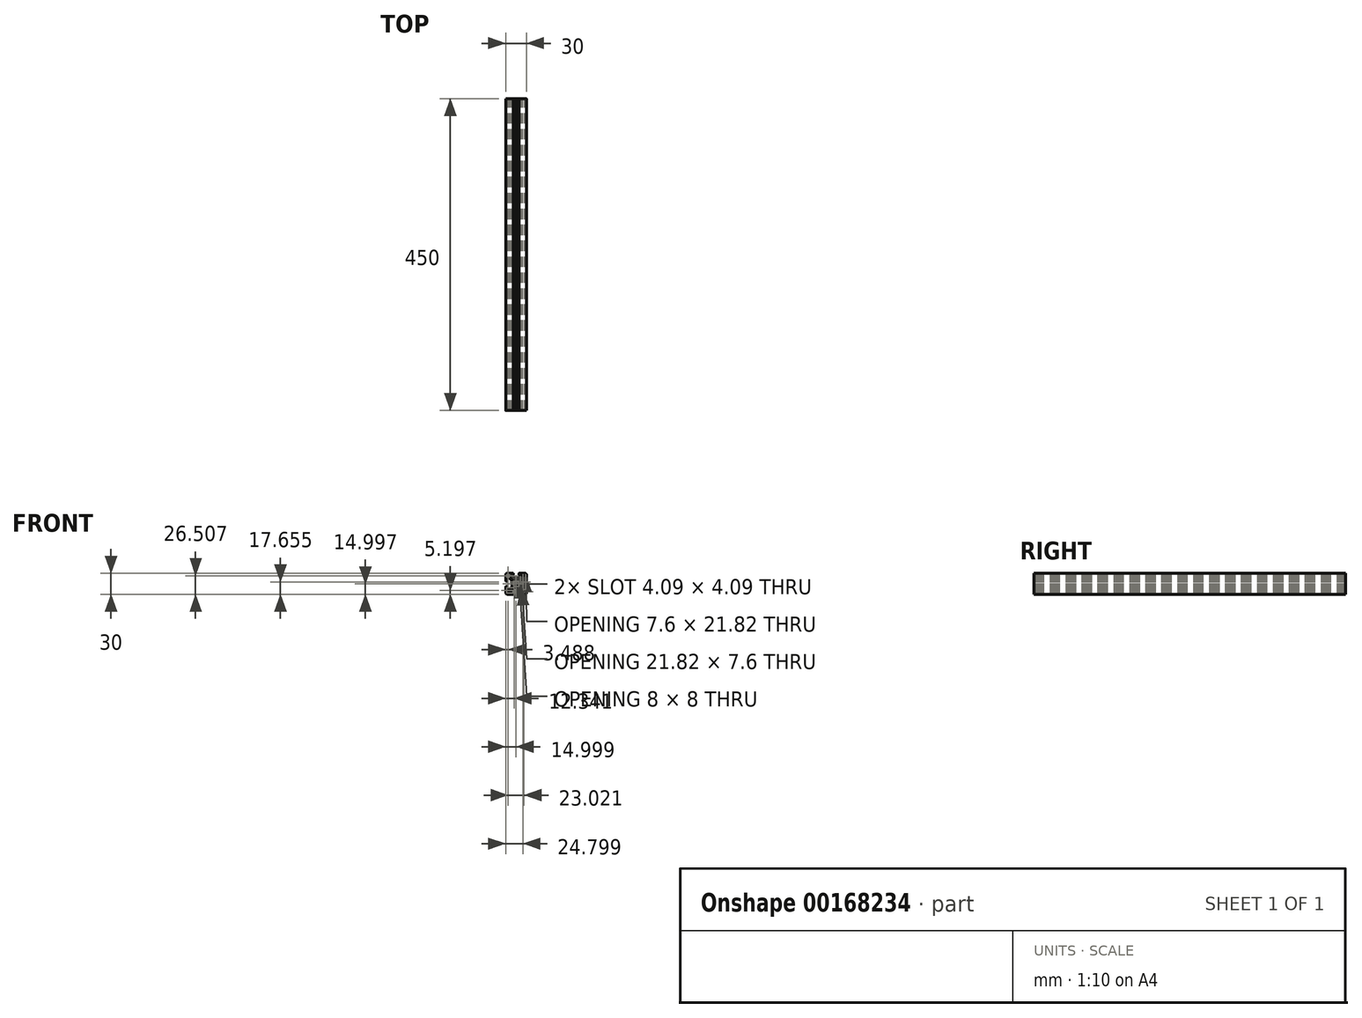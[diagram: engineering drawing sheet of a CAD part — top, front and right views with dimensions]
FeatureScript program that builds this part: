
annotation { "Feature Type Name" : "Feature", "Feature Type Description" : "" }
export const myFeature = defineFeature(function(context is Context, id is Id, definition is map)
    precondition{}
    {
        {
            var Q0;
            Q0=qCreatedBy(makeId("Front.planeOp"),FACE);
            var sketch = newSketch(context, id + "F0", { "sketchPlane" : qUnion([Q0])});
            skLineSegment(sketch, "E0", {"start": v(-39.84, 24.25) * mm, "end": v(-39.84, -9.75) * mm});
            skLineSegment(sketch, "E1", {"start": v(-56.84, 7.25) * mm, "end": v(-22.84, 7.25) * mm});
            skLineSegment(sketch, "E2", {"start": v(-52.84, 22.25) * mm, "end": v(-44.14, 22.25) * mm});
            skLineSegment(sketch, "E3", {"start": v(-52.84, -7.75) * mm, "end": v(-26.84, -7.75) * mm});
            skLineSegment(sketch, "E4", {"start": v(-24.84, 20.25) * mm, "end": v(-24.84, -5.75) * mm});
            skLineSegment(sketch, "E5", {"start": v(-54.84, 20.25) * mm, "end": v(-54.84, 11.55) * mm});
            skArc(sketch, "E6", {"start": v(-24.84, 20.25) * mm, "mid": v(-25.43, 21.66) * mm, "end": v(-26.84, 22.25) * mm});
            skArc(sketch, "E7", {"start": v(-52.84, 22.25) * mm, "mid": v(-54.26, 21.66) * mm, "end": v(-54.84, 20.25) * mm});
            skArc(sketch, "E8", {"start": v(-54.84, -5.75) * mm, "mid": v(-54.26, -7.17) * mm, "end": v(-52.84, -7.75) * mm});
            skArc(sketch, "E9", {"start": v(-26.84, -7.75) * mm, "mid": v(-25.43, -7.17) * mm, "end": v(-24.84, -5.75) * mm});
            skLineSegment(sketch, "E10", {"start": v(-52.84, -1) * mm, "end": v(-52.84, 2.95) * mm});
            skLineSegment(sketch, "E11", {"start": v(-26.84, 15.44) * mm, "end": v(-26.84, 0) * mm});
            skLineSegment(sketch, "E12", {"start": v(-48.03, -5.75) * mm, "end": v(-32.6, -5.75) * mm});
            skLineSegment(sketch, "E13", {"start": v(-54.54, 3.25) * mm, "end": v(-53.14, 3.25) * mm});
            skLineSegment(sketch, "E14", {"start": v(-54.54, 11.25) * mm, "end": v(-53.14, 11.25) * mm});
            skLineSegment(sketch, "E15", {"start": v(-52.84, 11.55) * mm, "end": v(-52.84, 15.5) * mm});
            skLineSegment(sketch, "E16", {"start": v(-35.54, 22.25) * mm, "end": v(-26.84, 22.25) * mm});
            skLineSegment(sketch, "E17", {"start": v(-49.5, -1) * mm, "end": v(-52.84, -1) * mm});
            skLineSegment(sketch, "E18", {"start": v(-49.5, 15.5) * mm, "end": v(-52.84, 15.5) * mm});
            skLineSegment(sketch, "E19", {"start": v(-35.26, 13.25) * mm, "end": v(-39.19, 13.25) * mm});
            skLineSegment(sketch, "E20", {"start": v(-35.67, 1.25) * mm, "end": v(-44.01, 1.25) * mm});
            skLineSegment(sketch, "E21", {"start": v(-33.84, 3.08) * mm, "end": v(-33.84, 11.42) * mm});
            skLineSegment(sketch, "E22", {"start": v(-45.84, 2.66) * mm, "end": v(-45.84, 4.75) * mm});
            skLineSegment(sketch, "E23", {"start": v(-44.43, 13.25) * mm, "end": v(-48.1, 16.91) * mm});
            skLineSegment(sketch, "E24", {"start": v(-45.84, 11.83) * mm, "end": v(-49.5, 15.5) * mm});
            skLineSegment(sketch, "E25", {"start": v(-33.55, 12.13) * mm, "end": v(-30.68, 14.99) * mm});
            skLineSegment(sketch, "E26", {"start": v(-35.26, 13.25) * mm, "end": v(-31.6, 16.91) * mm});
            skLineSegment(sketch, "E27", {"start": v(-33.55, 2.37) * mm, "end": v(-30.47, -0.71) * mm});
            skLineSegment(sketch, "E28", {"start": v(-34.96, 0.95) * mm, "end": v(-31.88, -2.12) * mm});
            skLineSegment(sketch, "E29", {"start": v(-44.72, 0.95) * mm, "end": v(-47.58, -1.91) * mm});
            skLineSegment(sketch, "E30", {"start": v(-45.84, 2.66) * mm, "end": v(-49.5, -1) * mm});
            skLineSegment(sketch, "E31", {"start": v(-54.84, 2.95) * mm, "end": v(-54.84, -5.75) * mm});
            skLineSegment(sketch, "E32", {"start": v(-43.84, 21.95) * mm, "end": v(-43.84, 20.55) * mm});
            skLineSegment(sketch, "E33", {"start": v(-35.84, 21.95) * mm, "end": v(-35.84, 20.55) * mm});
            skLineSegment(sketch, "E34", {"start": v(-31.6, 16.91) * mm, "end": v(-31.6, 20.25) * mm});
            skLineSegment(sketch, "E35", {"start": v(-48.1, 16.91) * mm, "end": v(-48.1, 20.25) * mm});
            skLineSegment(sketch, "E36", {"start": v(-44.14, 20.25) * mm, "end": v(-48.1, 20.25) * mm});
            skLineSegment(sketch, "E37", {"start": v(-35.54, 20.25) * mm, "end": v(-31.6, 20.25) * mm});
            skLineSegment(sketch, "E38", {"start": v(-30.4, 15.7) * mm, "end": v(-30.4, 18.32) * mm});
            skLineSegment(sketch, "E39", {"start": v(-30.4, 18.32) * mm, "end": v(-29.93, 19.6) * mm});
            skArc(sketch, "E40", {"start": v(-27.06, 17.38) * mm, "mid": v(-26.98, 20.45) * mm, "end": v(-29.93, 19.6) * mm});
            skArc(sketch, "E41", {"start": v(-27.06, 17.38) * mm, "mid": v(-27.5, 16.52) * mm, "end": v(-27, 15.7) * mm});
            skArc(sketch, "E42", {"start": v(-26.84, 15.44) * mm, "mid": v(-26.88, 15.59) * mm, "end": v(-27, 15.7) * mm});
            skArc(sketch, "E43", {"start": v(-49.76, 19.6) * mm, "mid": v(-52.88, 20.3) * mm, "end": v(-52.2, 17.16) * mm});
            skLineSegment(sketch, "E44", {"start": v(-49.39, 18.59) * mm, "end": v(-49.76, 19.6) * mm});
            skLineSegment(sketch, "E45", {"start": v(-51.18, 16.8) * mm, "end": v(-52.2, 17.16) * mm});
            skArc(sketch, "E46", {"start": v(-51.18, 16.8) * mm, "mid": v(-49.71, 17.12) * mm, "end": v(-49.39, 18.59) * mm});
            skArc(sketch, "E47", {"start": v(-29.93, -5.1) * mm, "mid": v(-26.8, -5.8) * mm, "end": v(-27.5, -2.67) * mm});
            skLineSegment(sketch, "E48", {"start": v(-28.5, -2.3) * mm, "end": v(-27.5, -2.67) * mm});
            skLineSegment(sketch, "E49", {"start": v(-30.3, -4.1) * mm, "end": v(-29.93, -5.1) * mm});
            skArc(sketch, "E50", {"start": v(-28.5, -2.3) * mm, "mid": v(-29.97, -2.63) * mm, "end": v(-30.3, -4.1) * mm});
            skArc(sketch, "E51", {"start": v(-33.55, 12.13) * mm, "mid": v(-33.76, 11.8) * mm, "end": v(-33.84, 11.42) * mm});
            skArc(sketch, "E52", {"start": v(-33.84, 3.08) * mm, "mid": v(-33.76, 2.7) * mm, "end": v(-33.55, 2.37) * mm});
            skLineSegment(sketch, "E53", {"start": v(-29.76, -1) * mm, "end": v(-27.84, -1) * mm});
            skArc(sketch, "E54", {"start": v(-30.47, -0.71) * mm, "mid": v(-30.15, -0.93) * mm, "end": v(-29.76, -1) * mm});
            skArc(sketch, "E55", {"start": v(-27.84, -1) * mm, "mid": v(-27.13, -0.71) * mm, "end": v(-26.84, 0) * mm});
            skArc(sketch, "E56", {"start": v(-30.68, 14.99) * mm, "mid": v(-30.47, 15.31) * mm, "end": v(-30.4, 15.7) * mm});
            skLineSegment(sketch, "E57", {"start": v(-31.6, -2.83) * mm, "end": v(-31.6, -4.75) * mm});
            skLineSegment(sketch, "E58", {"start": v(-48.3, -2.2) * mm, "end": v(-50.91, -2.2) * mm});
            skLineSegment(sketch, "E59", {"start": v(-50.91, -2.2) * mm, "end": v(-52.2, -2.67) * mm});
            skArc(sketch, "E60", {"start": v(-52.2, -2.67) * mm, "mid": v(-53.04, -5.61) * mm, "end": v(-49.98, -5.53) * mm});
            skArc(sketch, "E61", {"start": v(-48.29, -5.6) * mm, "mid": v(-49.12, -5.1) * mm, "end": v(-49.98, -5.53) * mm});
            skArc(sketch, "E62", {"start": v(-48.29, -5.6) * mm, "mid": v(-48.18, -5.71) * mm, "end": v(-48.03, -5.75) * mm});
            skArc(sketch, "E63", {"start": v(-48.3, -2.2) * mm, "mid": v(-47.9, -2.13) * mm, "end": v(-47.58, -1.91) * mm});
            skArc(sketch, "E64", {"start": v(-44.01, 1.25) * mm, "mid": v(-44.4, 1.17) * mm, "end": v(-44.72, 0.95) * mm});
            skArc(sketch, "E65", {"start": v(-34.96, 0.95) * mm, "mid": v(-35.29, 1.17) * mm, "end": v(-35.67, 1.25) * mm});
            skArc(sketch, "E66", {"start": v(-31.6, -2.83) * mm, "mid": v(-31.67, -2.45) * mm, "end": v(-31.88, -2.12) * mm});
            skArc(sketch, "E67", {"start": v(-32.6, -5.75) * mm, "mid": v(-31.88, -5.46) * mm, "end": v(-31.6, -4.75) * mm});
            skLineSegment(sketch, "E68", {"start": v(-36.34, 11.25) * mm, "end": v(-37.85, 11.25) * mm});
            skLineSegment(sketch, "E69", {"start": v(-35.84, 3.75) * mm, "end": v(-35.84, 5.25) * mm});
            skLineSegment(sketch, "E70", {"start": v(-36.34, 3.25) * mm, "end": v(-37.85, 3.25) * mm});
            skLineSegment(sketch, "E71", {"start": v(-43.84, 3.75) * mm, "end": v(-43.84, 5.25) * mm});
            skLineSegment(sketch, "E72", {"start": v(-42.34, 13.25) * mm, "end": v(-41.06, 13) * mm});
            skLineSegment(sketch, "E73", {"start": v(-39.84, 12.95) * mm, "end": v(-40.24, 13.18) * mm});
            skLineSegment(sketch, "E74", {"start": v(-39.84, 12.95) * mm, "end": v(-39.44, 13.18) * mm});
            skLineSegment(sketch, "E75", {"start": v(-42.34, 13.25) * mm, "end": v(-44.43, 13.25) * mm});
            skArc(sketch, "E76", {"start": v(-39.19, 13.25) * mm, "mid": v(-39.32, 13.23) * mm, "end": v(-39.44, 13.18) * mm});
            skArc(sketch, "E77", {"start": v(-40.24, 13.18) * mm, "mid": v(-40.5, 13.25) * mm, "end": v(-40.74, 13.18) * mm});
            skLineSegment(sketch, "E78", {"start": v(-41.06, 13) * mm, "end": v(-40.74, 13.18) * mm});
            skArc(sketch, "E79", {"start": v(-45.84, 7.9) * mm, "mid": v(-45.82, 7.77) * mm, "end": v(-45.77, 7.65) * mm});
            skLineSegment(sketch, "E80", {"start": v(-45.84, 4.75) * mm, "end": v(-45.6, 6.03) * mm});
            skLineSegment(sketch, "E81", {"start": v(-45.54, 7.25) * mm, "end": v(-45.77, 6.84) * mm});
            skLineSegment(sketch, "E82", {"start": v(-45.54, 7.25) * mm, "end": v(-45.77, 7.65) * mm});
            skArc(sketch, "E83", {"start": v(-45.77, 6.84) * mm, "mid": v(-45.84, 6.6) * mm, "end": v(-45.77, 6.34) * mm});
            skLineSegment(sketch, "E84", {"start": v(-45.6, 6.03) * mm, "end": v(-45.77, 6.34) * mm});
            skLineSegment(sketch, "E85", {"start": v(-45.84, 7.9) * mm, "end": v(-45.84, 11.83) * mm});
            skArc(sketch, "E86", {"start": v(-35.84, 20.55) * mm, "mid": v(-35.75, 20.33) * mm, "end": v(-35.54, 20.25) * mm});
            skArc(sketch, "E87", {"start": v(-35.54, 22.25) * mm, "mid": v(-35.75, 22.16) * mm, "end": v(-35.84, 21.95) * mm});
            skArc(sketch, "E88", {"start": v(-44.14, 20.25) * mm, "mid": v(-43.93, 20.33) * mm, "end": v(-43.84, 20.55) * mm});
            skArc(sketch, "E89", {"start": v(-43.84, 21.95) * mm, "mid": v(-43.93, 22.16) * mm, "end": v(-44.14, 22.25) * mm});
            skArc(sketch, "E90", {"start": v(-53.14, 11.25) * mm, "mid": v(-52.93, 11.33) * mm, "end": v(-52.84, 11.55) * mm});
            skArc(sketch, "E91", {"start": v(-54.84, 11.55) * mm, "mid": v(-54.75, 11.33) * mm, "end": v(-54.54, 11.25) * mm});
            skArc(sketch, "E92", {"start": v(-52.84, 2.95) * mm, "mid": v(-52.93, 3.16) * mm, "end": v(-53.14, 3.25) * mm});
            skArc(sketch, "E93", {"start": v(-54.54, 3.25) * mm, "mid": v(-54.75, 3.16) * mm, "end": v(-54.84, 2.95) * mm});
            skArc(sketch, "E94", {"start": v(-38.85, 10.5) * mm, "mid": v(-39.84, 10.65) * mm, "end": v(-40.83, 10.5) * mm});
            skArc(sketch, "E95", {"start": v(-41.34, 10.82) * mm, "mid": v(-41.16, 10.54) * mm, "end": v(-40.83, 10.5) * mm});
            skArc(sketch, "E96", {"start": v(-41.34, 10.82) * mm, "mid": v(-41.5, 11.13) * mm, "end": v(-41.84, 11.25) * mm});
            skArc(sketch, "E97", {"start": v(-38.85, 10.5) * mm, "mid": v(-38.52, 10.54) * mm, "end": v(-38.34, 10.82) * mm});
            skArc(sketch, "E98", {"start": v(-37.85, 11.25) * mm, "mid": v(-38.17, 11.13) * mm, "end": v(-38.34, 10.82) * mm});
            skLineSegment(sketch, "E99", {"start": v(-41.84, 11.25) * mm, "end": v(-43.34, 11.25) * mm});
            skArc(sketch, "E100", {"start": v(-43.34, 11.25) * mm, "mid": v(-43.7, 11.1) * mm, "end": v(-43.84, 10.75) * mm});
            skArc(sketch, "E101", {"start": v(-35.84, 10.75) * mm, "mid": v(-35.99, 11.1) * mm, "end": v(-36.34, 11.25) * mm});
            skArc(sketch, "E102", {"start": v(-36.34, 3.25) * mm, "mid": v(-35.99, 3.4) * mm, "end": v(-35.84, 3.75) * mm});
            skArc(sketch, "E103", {"start": v(-43.84, 3.75) * mm, "mid": v(-43.7, 3.4) * mm, "end": v(-43.34, 3.25) * mm});
            skArc(sketch, "E104", {"start": v(-43.1, 8.23) * mm, "mid": v(-43.24, 7.25) * mm, "end": v(-43.1, 6.26) * mm});
            skArc(sketch, "E105", {"start": v(-43.42, 5.75) * mm, "mid": v(-43.14, 5.93) * mm, "end": v(-43.1, 6.26) * mm});
            skArc(sketch, "E106", {"start": v(-43.42, 5.75) * mm, "mid": v(-43.72, 5.58) * mm, "end": v(-43.84, 5.25) * mm});
            skArc(sketch, "E107", {"start": v(-43.1, 8.23) * mm, "mid": v(-43.14, 8.56) * mm, "end": v(-43.42, 8.75) * mm});
            skArc(sketch, "E108", {"start": v(-43.84, 9.24) * mm, "mid": v(-43.72, 8.92) * mm, "end": v(-43.42, 8.75) * mm});
            skArc(sketch, "E109", {"start": v(-36.59, 6.26) * mm, "mid": v(-36.44, 7.25) * mm, "end": v(-36.59, 8.23) * mm});
            skArc(sketch, "E110", {"start": v(-36.27, 8.75) * mm, "mid": v(-36.54, 8.56) * mm, "end": v(-36.59, 8.23) * mm});
            skArc(sketch, "E111", {"start": v(-36.27, 8.75) * mm, "mid": v(-35.96, 8.92) * mm, "end": v(-35.84, 9.24) * mm});
            skArc(sketch, "E112", {"start": v(-36.59, 6.26) * mm, "mid": v(-36.54, 5.93) * mm, "end": v(-36.27, 5.75) * mm});
            skArc(sketch, "E113", {"start": v(-35.84, 5.25) * mm, "mid": v(-35.96, 5.58) * mm, "end": v(-36.27, 5.75) * mm});
            skArc(sketch, "E114", {"start": v(-40.83, 4) * mm, "mid": v(-39.84, 3.85) * mm, "end": v(-38.85, 4) * mm});
            skArc(sketch, "E115", {"start": v(-40.83, 4) * mm, "mid": v(-41.16, 3.95) * mm, "end": v(-41.34, 3.67) * mm});
            skArc(sketch, "E116", {"start": v(-41.84, 3.25) * mm, "mid": v(-41.5, 3.37) * mm, "end": v(-41.34, 3.67) * mm});
            skArc(sketch, "E117", {"start": v(-38.34, 3.67) * mm, "mid": v(-38.52, 3.95) * mm, "end": v(-38.85, 4) * mm});
            skArc(sketch, "E118", {"start": v(-38.34, 3.67) * mm, "mid": v(-38.17, 3.37) * mm, "end": v(-37.85, 3.25) * mm});
            skLineSegment(sketch, "E119", {"start": v(-35.84, 9.24) * mm, "end": v(-35.84, 10.75) * mm});
            skLineSegment(sketch, "E120", {"start": v(-41.84, 3.25) * mm, "end": v(-43.34, 3.25) * mm});
            skLineSegment(sketch, "E121", {"start": v(-43.84, 9.24) * mm, "end": v(-43.84, 10.75) * mm});
            skCircle(sketch, "E122", {"center": v(-39.84, 7.25) * mm, "radius": 3.4 * mm});
            skLineSegment(sketch, "E123", {"start": v(-28.14, 22.85) * mm, "end": v(-28.14, 15.05) * mm});
            skLineSegment(sketch, "E124", {"start": v(-32.04, 18.95) * mm, "end": v(-24.24, 18.95) * mm});
            skLineSegment(sketch, "E125", {"start": v(-28.14, -0.55) * mm, "end": v(-28.14, -8.35) * mm});
            skLineSegment(sketch, "E126", {"start": v(-32.04, -4.45) * mm, "end": v(-24.24, -4.45) * mm});
            skLineSegment(sketch, "E127", {"start": v(-51.54, -0.55) * mm, "end": v(-51.54, -8.35) * mm});
            skLineSegment(sketch, "E128", {"start": v(-55.44, -4.45) * mm, "end": v(-47.64, -4.45) * mm});
            skLineSegment(sketch, "E129", {"start": v(-51.54, 22.85) * mm, "end": v(-51.54, 15.05) * mm});
            skLineSegment(sketch, "E130", {"start": v(-55.44, 18.95) * mm, "end": v(-47.64, 18.95) * mm});
            skSolve(sketch);
        }
        {
            var Q0;
            Q0=qCreatedBy(makeId("Front.planeOp"),FACE);
            var sketch = newSketch(context, id + "F1", { "sketchPlane" : qUnion([Q0])});
            skArc(sketch, "E131.0", {"start": v(-48.29, -5.6) * mm, "mid": v(-49.12, -5.1) * mm, "end": v(-49.98, -5.53) * mm});
            skLineSegment(sketch, "E131.1", {"start": v(-44.72, 0.95) * mm, "end": v(-47.58, -1.91) * mm});
            skLineSegment(sketch, "E131.3", {"start": v(-35.67, 1.25) * mm, "end": v(-44.01, 1.25) * mm});
            skLineSegment(sketch, "E131.4", {"start": v(-44.14, 20.25) * mm, "end": v(-48.1, 20.25) * mm});
            skArc(sketch, "E131.5", {"start": v(-51.18, 16.8) * mm, "mid": v(-49.71, 17.12) * mm, "end": v(-49.39, 18.59) * mm});
            skLineSegment(sketch, "E131.6", {"start": v(-45.84, 2.66) * mm, "end": v(-49.5, -1) * mm});
            skLineSegment(sketch, "E131.7", {"start": v(-33.84, 3.08) * mm, "end": v(-33.84, 11.42) * mm});
            skLineSegment(sketch, "E131.8", {"start": v(-45.84, 7.9) * mm, "end": v(-45.84, 11.83) * mm});
            skLineSegment(sketch, "E131.9", {"start": v(-35.54, 20.25) * mm, "end": v(-31.6, 20.25) * mm});
            skLineSegment(sketch, "E131.10", {"start": v(-45.84, 2.66) * mm, "end": v(-45.84, 4.75) * mm});
            skLineSegment(sketch, "E131.11", {"start": v(-30.4, 15.7) * mm, "end": v(-30.4, 18.32) * mm});
            skLineSegment(sketch, "E131.12", {"start": v(-44.43, 13.25) * mm, "end": v(-48.1, 16.91) * mm});
            skLineSegment(sketch, "E131.13", {"start": v(-48.1, 16.91) * mm, "end": v(-48.1, 20.25) * mm});
            skLineSegment(sketch, "E131.15", {"start": v(-31.6, 16.91) * mm, "end": v(-31.6, 20.25) * mm});
            skArc(sketch, "E131.16", {"start": v(-28.5, -2.3) * mm, "mid": v(-29.97, -2.63) * mm, "end": v(-30.3, -4.1) * mm});
            skLineSegment(sketch, "E131.17", {"start": v(-49.5, 15.5) * mm, "end": v(-52.84, 15.5) * mm});
            skLineSegment(sketch, "E131.18", {"start": v(-35.26, 13.25) * mm, "end": v(-39.19, 13.25) * mm});
            skLineSegment(sketch, "E131.19", {"start": v(-48.03, -5.75) * mm, "end": v(-32.6, -5.75) * mm});
            skLineSegment(sketch, "E131.20", {"start": v(-26.84, 15.44) * mm, "end": v(-26.84, 0) * mm});
            skLineSegment(sketch, "E131.21", {"start": v(-52.84, -1) * mm, "end": v(-52.84, 2.95) * mm});
            skArc(sketch, "E131.23", {"start": v(-26.84, -7.75) * mm, "mid": v(-25.43, -7.17) * mm, "end": v(-24.84, -5.75) * mm});
            skArc(sketch, "E131.24", {"start": v(-54.84, -5.75) * mm, "mid": v(-54.26, -7.17) * mm, "end": v(-52.84, -7.75) * mm});
            skArc(sketch, "E131.25", {"start": v(-52.84, 22.25) * mm, "mid": v(-54.26, 21.66) * mm, "end": v(-54.84, 20.25) * mm});
            skArc(sketch, "E131.26", {"start": v(-24.84, 20.25) * mm, "mid": v(-25.43, 21.66) * mm, "end": v(-26.84, 22.25) * mm});
            skLineSegment(sketch, "E131.27", {"start": v(-54.84, 20.25) * mm, "end": v(-54.84, 11.55) * mm});
            skLineSegment(sketch, "E131.28", {"start": v(-24.84, 20.25) * mm, "end": v(-24.84, -5.75) * mm});
            skLineSegment(sketch, "E131.29", {"start": v(-49.5, -1) * mm, "end": v(-52.84, -1) * mm});
            skLineSegment(sketch, "E131.30", {"start": v(-52.84, -7.75) * mm, "end": v(-26.84, -7.75) * mm});
            skLineSegment(sketch, "E131.31", {"start": v(-52.84, 22.25) * mm, "end": v(-44.14, 22.25) * mm});
            skLineSegment(sketch, "E131.32", {"start": v(-52.84, 11.55) * mm, "end": v(-52.84, 15.5) * mm});
            skLineSegment(sketch, "E131.33", {"start": v(-34.96, 0.95) * mm, "end": v(-31.88, -2.12) * mm});
            skArc(sketch, "E131.34", {"start": v(-52.2, -2.67) * mm, "mid": v(-53.04, -5.61) * mm, "end": v(-49.98, -5.53) * mm});
            skLineSegment(sketch, "E131.35", {"start": v(-42.34, 13.25) * mm, "end": v(-44.43, 13.25) * mm});
            skLineSegment(sketch, "E131.37", {"start": v(-33.55, 2.37) * mm, "end": v(-30.47, -0.71) * mm});
            skArc(sketch, "E131.38", {"start": v(-49.76, 19.6) * mm, "mid": v(-52.88, 20.3) * mm, "end": v(-52.2, 17.16) * mm});
            skLineSegment(sketch, "E131.39", {"start": v(-35.54, 22.25) * mm, "end": v(-26.84, 22.25) * mm});
            skLineSegment(sketch, "E131.41", {"start": v(-35.26, 13.25) * mm, "end": v(-31.6, 16.91) * mm});
            skLineSegment(sketch, "E131.42", {"start": v(-48.3, -2.2) * mm, "end": v(-50.91, -2.2) * mm});
            skLineSegment(sketch, "E131.43", {"start": v(-33.55, 12.13) * mm, "end": v(-30.68, 14.99) * mm});
            skLineSegment(sketch, "E131.46", {"start": v(-54.84, 2.95) * mm, "end": v(-54.84, -5.75) * mm});
            skArc(sketch, "E131.47", {"start": v(-29.93, -5.1) * mm, "mid": v(-26.8, -5.8) * mm, "end": v(-27.5, -2.67) * mm});
            skLineSegment(sketch, "E131.48", {"start": v(-45.84, 11.83) * mm, "end": v(-49.5, 15.5) * mm});
            skArc(sketch, "E131.49", {"start": v(-27.06, 17.38) * mm, "mid": v(-26.98, 20.45) * mm, "end": v(-29.93, 19.6) * mm});
            skArc(sketch, "E131.50", {"start": v(-36.59, 6.26) * mm, "mid": v(-36.44, 7.25) * mm, "end": v(-36.59, 8.23) * mm});
            skArc(sketch, "E131.51", {"start": v(-38.85, 10.5) * mm, "mid": v(-39.84, 10.65) * mm, "end": v(-40.83, 10.5) * mm});
            skArc(sketch, "E131.52", {"start": v(-40.83, 4) * mm, "mid": v(-39.84, 3.85) * mm, "end": v(-38.85, 4) * mm});
            skLineSegment(sketch, "E131.53", {"start": v(-31.6, -2.83) * mm, "end": v(-31.6, -4.75) * mm});
            skArc(sketch, "E131.54", {"start": v(-43.1, 8.23) * mm, "mid": v(-43.24, 7.25) * mm, "end": v(-43.1, 6.26) * mm});
            skArc(sketch, "E131.55", {"start": v(-40.83, 4) * mm, "mid": v(-41.16, 3.95) * mm, "end": v(-41.34, 3.67) * mm});
            skLineSegment(sketch, "E131.56", {"start": v(-51.18, 16.8) * mm, "end": v(-52.2, 17.16) * mm});
            skLineSegment(sketch, "E131.57", {"start": v(-41.84, 11.25) * mm, "end": v(-43.34, 11.25) * mm});
            skLineSegment(sketch, "E131.58", {"start": v(-36.34, 11.25) * mm, "end": v(-37.85, 11.25) * mm});
            skArc(sketch, "E131.59", {"start": v(-33.84, 3.08) * mm, "mid": v(-33.76, 2.7) * mm, "end": v(-33.55, 2.37) * mm});
            skArc(sketch, "E131.60", {"start": v(-41.84, 3.25) * mm, "mid": v(-41.5, 3.37) * mm, "end": v(-41.34, 3.67) * mm});
            skArc(sketch, "E131.61", {"start": v(-43.34, 11.25) * mm, "mid": v(-43.7, 11.1) * mm, "end": v(-43.84, 10.75) * mm});
            skArc(sketch, "E131.62", {"start": v(-36.27, 8.75) * mm, "mid": v(-36.54, 8.56) * mm, "end": v(-36.59, 8.23) * mm});
            skLineSegment(sketch, "E131.63", {"start": v(-35.84, 3.75) * mm, "end": v(-35.84, 5.25) * mm});
            skLineSegment(sketch, "E131.64", {"start": v(-29.76, -1) * mm, "end": v(-27.84, -1) * mm});
            skArc(sketch, "E131.65", {"start": v(-38.34, 3.67) * mm, "mid": v(-38.52, 3.95) * mm, "end": v(-38.85, 4) * mm});
            skArc(sketch, "E131.66", {"start": v(-35.84, 10.75) * mm, "mid": v(-35.99, 11.1) * mm, "end": v(-36.34, 11.25) * mm});
            skArc(sketch, "E131.67", {"start": v(-35.84, 20.55) * mm, "mid": v(-35.75, 20.33) * mm, "end": v(-35.54, 20.25) * mm});
            skLineSegment(sketch, "E131.68", {"start": v(-36.34, 3.25) * mm, "end": v(-37.85, 3.25) * mm});
            skArc(sketch, "E131.69", {"start": v(-30.47, -0.71) * mm, "mid": v(-30.15, -0.93) * mm, "end": v(-29.76, -1) * mm});
            skArc(sketch, "E131.70", {"start": v(-38.34, 3.67) * mm, "mid": v(-38.17, 3.37) * mm, "end": v(-37.85, 3.25) * mm});
            skArc(sketch, "E131.71", {"start": v(-36.34, 3.25) * mm, "mid": v(-35.99, 3.4) * mm, "end": v(-35.84, 3.75) * mm});
            skArc(sketch, "E131.72", {"start": v(-27.84, -1) * mm, "mid": v(-27.13, -0.71) * mm, "end": v(-26.84, 0) * mm});
            skLineSegment(sketch, "E131.73", {"start": v(-30.4, 18.32) * mm, "end": v(-29.93, 19.6) * mm});
            skLineSegment(sketch, "E131.74", {"start": v(-35.84, 9.24) * mm, "end": v(-35.84, 10.75) * mm});
            skArc(sketch, "E131.75", {"start": v(-43.84, 3.75) * mm, "mid": v(-43.7, 3.4) * mm, "end": v(-43.34, 3.25) * mm});
            skArc(sketch, "E131.76", {"start": v(-35.54, 22.25) * mm, "mid": v(-35.75, 22.16) * mm, "end": v(-35.84, 21.95) * mm});
            skLineSegment(sketch, "E131.77", {"start": v(-43.84, 3.75) * mm, "end": v(-43.84, 5.25) * mm});
            skArc(sketch, "E131.78", {"start": v(-31.6, -2.83) * mm, "mid": v(-31.67, -2.45) * mm, "end": v(-31.88, -2.12) * mm});
            skArc(sketch, "E131.79", {"start": v(-48.3, -2.2) * mm, "mid": v(-47.9, -2.13) * mm, "end": v(-47.58, -1.91) * mm});
            skArc(sketch, "E131.80", {"start": v(-33.55, 12.13) * mm, "mid": v(-33.76, 11.8) * mm, "end": v(-33.84, 11.42) * mm});
            skArc(sketch, "E131.81", {"start": v(-32.6, -5.75) * mm, "mid": v(-31.88, -5.46) * mm, "end": v(-31.6, -4.75) * mm});
            skLineSegment(sketch, "E131.82", {"start": v(-35.84, 21.95) * mm, "end": v(-35.84, 20.55) * mm});
            skLineSegment(sketch, "E131.83", {"start": v(-30.3, -4.1) * mm, "end": v(-29.93, -5.1) * mm});
            skArc(sketch, "E131.84", {"start": v(-34.96, 0.95) * mm, "mid": v(-35.29, 1.17) * mm, "end": v(-35.67, 1.25) * mm});
            skArc(sketch, "E131.85", {"start": v(-39.19, 13.25) * mm, "mid": v(-39.32, 13.23) * mm, "end": v(-39.44, 13.18) * mm});
            skArc(sketch, "E131.86", {"start": v(-43.84, 9.24) * mm, "mid": v(-43.72, 8.92) * mm, "end": v(-43.42, 8.75) * mm});
            skLineSegment(sketch, "E131.87", {"start": v(-49.39, 18.59) * mm, "end": v(-49.76, 19.6) * mm});
            skArc(sketch, "E131.88", {"start": v(-43.1, 8.23) * mm, "mid": v(-43.14, 8.56) * mm, "end": v(-43.42, 8.75) * mm});
            skLineSegment(sketch, "E131.89", {"start": v(-50.91, -2.2) * mm, "end": v(-52.2, -2.67) * mm});
            skLineSegment(sketch, "E131.90", {"start": v(-28.5, -2.3) * mm, "end": v(-27.5, -2.67) * mm});
            skArc(sketch, "E131.91", {"start": v(-44.01, 1.25) * mm, "mid": v(-44.4, 1.17) * mm, "end": v(-44.72, 0.95) * mm});
            skLineSegment(sketch, "E131.92", {"start": v(-45.84, 4.75) * mm, "end": v(-45.6, 6.03) * mm});
            skArc(sketch, "E131.93", {"start": v(-26.84, 15.44) * mm, "mid": v(-26.88, 15.59) * mm, "end": v(-27, 15.7) * mm});
            skLineSegment(sketch, "E131.94", {"start": v(-43.84, 9.24) * mm, "end": v(-43.84, 10.75) * mm});
            skArc(sketch, "E131.95", {"start": v(-27.06, 17.38) * mm, "mid": v(-27.5, 16.52) * mm, "end": v(-27, 15.7) * mm});
            skArc(sketch, "E131.96", {"start": v(-36.27, 8.75) * mm, "mid": v(-35.96, 8.92) * mm, "end": v(-35.84, 9.24) * mm});
            skLineSegment(sketch, "E131.97", {"start": v(-42.34, 13.25) * mm, "end": v(-41.06, 13) * mm});
            skLineSegment(sketch, "E131.98", {"start": v(-41.84, 3.25) * mm, "end": v(-43.34, 3.25) * mm});
            skArc(sketch, "E131.99", {"start": v(-30.68, 14.99) * mm, "mid": v(-30.47, 15.31) * mm, "end": v(-30.4, 15.7) * mm});
            skArc(sketch, "E131.100", {"start": v(-40.24, 13.18) * mm, "mid": v(-40.5, 13.25) * mm, "end": v(-40.74, 13.18) * mm});
            skLineSegment(sketch, "E131.101", {"start": v(-45.6, 6.03) * mm, "end": v(-45.77, 6.34) * mm});
            skLineSegment(sketch, "E131.102", {"start": v(-41.06, 13) * mm, "end": v(-40.74, 13.18) * mm});
            skArc(sketch, "E131.103", {"start": v(-48.29, -5.6) * mm, "mid": v(-48.18, -5.71) * mm, "end": v(-48.03, -5.75) * mm});
            skArc(sketch, "E131.104", {"start": v(-37.85, 11.25) * mm, "mid": v(-38.17, 11.13) * mm, "end": v(-38.34, 10.82) * mm});
            skArc(sketch, "E131.105", {"start": v(-38.85, 10.5) * mm, "mid": v(-38.52, 10.54) * mm, "end": v(-38.34, 10.82) * mm});
            skArc(sketch, "E131.106", {"start": v(-35.84, 5.25) * mm, "mid": v(-35.96, 5.58) * mm, "end": v(-36.27, 5.75) * mm});
            skLineSegment(sketch, "E131.107", {"start": v(-54.54, 11.25) * mm, "end": v(-53.14, 11.25) * mm});
            skArc(sketch, "E131.108", {"start": v(-54.84, 11.55) * mm, "mid": v(-54.75, 11.33) * mm, "end": v(-54.54, 11.25) * mm});
            skLineSegment(sketch, "E131.109", {"start": v(-39.84, 12.95) * mm, "end": v(-39.44, 13.18) * mm});
            skArc(sketch, "E131.110", {"start": v(-53.14, 11.25) * mm, "mid": v(-52.93, 11.33) * mm, "end": v(-52.84, 11.55) * mm});
            skArc(sketch, "E131.111", {"start": v(-43.42, 5.75) * mm, "mid": v(-43.72, 5.58) * mm, "end": v(-43.84, 5.25) * mm});
            skArc(sketch, "E131.112", {"start": v(-41.34, 10.82) * mm, "mid": v(-41.5, 11.13) * mm, "end": v(-41.84, 11.25) * mm});
            skLineSegment(sketch, "E131.113", {"start": v(-39.84, 12.95) * mm, "end": v(-40.24, 13.18) * mm});
            skArc(sketch, "E131.114", {"start": v(-43.42, 5.75) * mm, "mid": v(-43.14, 5.93) * mm, "end": v(-43.1, 6.26) * mm});
            skArc(sketch, "E131.115", {"start": v(-36.59, 6.26) * mm, "mid": v(-36.54, 5.93) * mm, "end": v(-36.27, 5.75) * mm});
            skArc(sketch, "E131.116", {"start": v(-41.34, 10.82) * mm, "mid": v(-41.16, 10.54) * mm, "end": v(-40.83, 10.5) * mm});
            skLineSegment(sketch, "E131.117", {"start": v(-45.54, 7.25) * mm, "end": v(-45.77, 7.65) * mm});
            skArc(sketch, "E131.118", {"start": v(-45.77, 6.84) * mm, "mid": v(-45.84, 6.6) * mm, "end": v(-45.77, 6.34) * mm});
            skLineSegment(sketch, "E131.119", {"start": v(-43.84, 21.95) * mm, "end": v(-43.84, 20.55) * mm});
            skArc(sketch, "E131.120", {"start": v(-43.84, 21.95) * mm, "mid": v(-43.93, 22.16) * mm, "end": v(-44.14, 22.25) * mm});
            skArc(sketch, "E131.121", {"start": v(-44.14, 20.25) * mm, "mid": v(-43.93, 20.33) * mm, "end": v(-43.84, 20.55) * mm});
            skArc(sketch, "E131.122", {"start": v(-54.54, 3.25) * mm, "mid": v(-54.75, 3.16) * mm, "end": v(-54.84, 2.95) * mm});
            skArc(sketch, "E131.123", {"start": v(-45.84, 7.9) * mm, "mid": v(-45.82, 7.77) * mm, "end": v(-45.77, 7.65) * mm});
            skLineSegment(sketch, "E131.124", {"start": v(-45.54, 7.25) * mm, "end": v(-45.77, 6.84) * mm});
            skLineSegment(sketch, "E131.125", {"start": v(-54.54, 3.25) * mm, "end": v(-53.14, 3.25) * mm});
            skArc(sketch, "E131.126", {"start": v(-52.84, 2.95) * mm, "mid": v(-52.93, 3.16) * mm, "end": v(-53.14, 3.25) * mm});
            skSolve(sketch);
        }
        {
            var Q0;
            Q0=makeQuery(id+"F1.imprint","IMPRINT",FACE,{"disambiguationData":[TD([[makeQuery(id+"F1.imprint","IMPRINT",EDGE,{"derivedFrom":sQuery(id+"F1.wireOp",EDGE,"E131.0")}),1.0]])]});
            extrude(context, id + "F2", {"entities" : qUnion([Q0]), "endBound" : BoundingType.SYMMETRIC, "depth" : 450 * mm});
        }
    });
